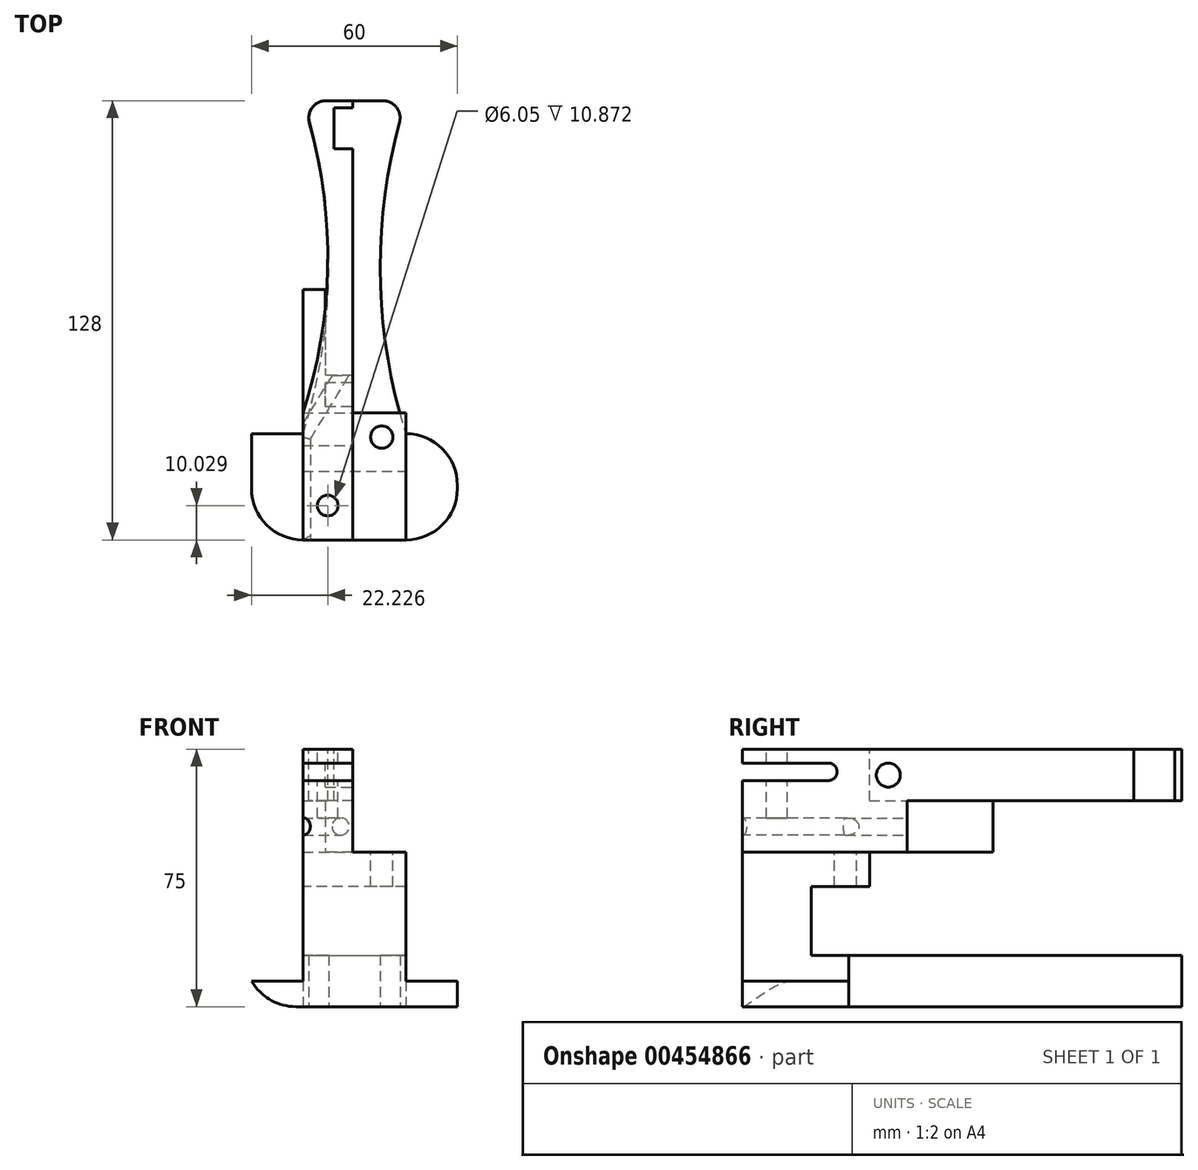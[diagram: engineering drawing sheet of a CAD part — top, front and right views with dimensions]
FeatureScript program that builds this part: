
annotation { "Feature Type Name" : "Feature", "Feature Type Description" : "" }
export const myFeature = defineFeature(function(context is Context, id is Id, definition is map)
    precondition{}
    {
        {
            var Q0;
            Q0=qCreatedBy(makeId("Top.planeOp"),FACE);
            var sketch = newSketch(context, id + "F0", { "sketchPlane" : qUnion([Q0])});
            skLineSegment(sketch, "E0", {"start": v(-15.87, -34.5) * mm, "end": v(-15.87, -0.5) * mm});
            skLineSegment(sketch, "E1", {"start": v(-15.87, -0.5) * mm, "end": v(-15.87, -0.5) * mm});
            skLineSegment(sketch, "E2", {"start": v(14.13, -0.5) * mm, "end": v(14.13, -34.5) * mm});
            skLineSegment(sketch, "E3", {"start": v(14.13, -34.5) * mm, "end": v(-15.87, -34.5) * mm});
            skLineSegment(sketch, "E4", {"start": v(-15.87, -0.5) * mm, "end": v(-15.87, 25.5) * mm});
            skLineSegment(sketch, "E5", {"start": v(-15.87, 25.5) * mm, "end": v(14.13, 25.5) * mm});
            skLineSegment(sketch, "E6", {"start": v(14.13, 25.5) * mm, "end": v(14.13, -0.5) * mm});
            skLineSegment(sketch, "E7.trimOffspring", {"start": v(14.13, -0.5) * mm, "end": v(14.13, -0.5) * mm});
            skLineSegment(sketch, "E8", {"start": v(-0.87, 25.5) * mm, "end": v(-0.87, -34.5) * mm, "construction": true});
            skSolve(sketch);
        }
        {
            var Q0;
            Q0=makeQuery(id+"F0.imprint","IMPRINT",FACE,{"disambiguationData":[TD([[makeQuery(id+"F0.imprint","IMPRINT",EDGE,{"derivedFrom":sQuery(id+"F0.wireOp",EDGE,"E0")}),-1.0]])]});
            extrude(context, id + "F1", {"entities" : qUnion([Q0]), "depth" : 15 * mm});
        }
        {
            var Q0;
            Q0=makeQuery(id+"F1.opExtrude","CAP_FACE",FACE,{"disambiguationData":[OSD([sQuery(id+"F0.wireOp",EDGE,"E0"),sQuery(id+"F0.wireOp",EDGE,"E1"),sQuery(id+"F0.wireOp",EDGE,"E2"),sQuery(id+"F0.wireOp",EDGE,"E3"),sQuery(id+"F0.wireOp",EDGE,"E4"),sQuery(id+"F0.wireOp",EDGE,"E5"),sQuery(id+"F0.wireOp",EDGE,"E6"),sQuery(id+"F0.wireOp",EDGE,"E7.trimOffspring"),sQuery(id+"F0.wireOp",EDGE,"9290abd9-eac5-44e8-944c-73c0075432f2")])],"isStart":false});
            var sketch = newSketch(context, id + "F2", { "sketchPlane" : qUnion([Q0])});
            skLineSegment(sketch, "E9", {"start": v(-15.87, -14.5) * mm, "end": v(14.13, -14.5) * mm});
            skSolve(sketch);
        }
        {
            var Q0;
            Q0 = qSketchRegion(id + "F2", true);
            var Q1;
            {var subQ0=sQuery(id+"F2.wireOp",EDGE,"E9");Q1=makeQuery(id+"F2.imprint","IMPRINT",FACE,{"disambiguationData":[TD([[makeQuery(id+"F2.imprint","IMPRINT",EDGE,{"derivedFrom":subQ0}),-1.0]])]});}
            extrude(context, id + "F3", {"entities" : qUnion([Q0, Q1]), "operationType" : NewBodyOperationType.ADD, "depth" : 30 * mm});
        }
        {
            var Q0;
            Q0=makeQuery(id+"F3.opExtrude","SWEPT_FACE",FACE,{"disambiguationData":[OSD([sQuery(id+"F2.wireOp",EDGE,"E9")])]});
            var sketch = newSketch(context, id + "F4", { "sketchPlane" : qUnion([Q0])});
            skLineSegment(sketch, "E10", {"start": v(-14.13, 35) * mm, "end": v(15.87, 35) * mm});
            skSolve(sketch);
        }
        {
            var Q0;
            {var subQ0=sQuery(id+"F4.wireOp",EDGE,"E10");Q0=makeQuery(id+"F4.imprint","IMPRINT",FACE,{"disambiguationData":[TD([[makeQuery(id+"F4.imprint","IMPRINT",EDGE,{"derivedFrom":subQ0}),1.0]])]});}
            extrude(context, id + "F5", {"entities" : qUnion([Q0]), "operationType" : NewBodyOperationType.ADD, "depth" : 17 * mm});
        }
        {
            var Q0;
            {var subQ0=sQuery(id+"F2.wireOp",EDGE,"E9");Q0=makeQuery(id+"F5.boolean.opBoolean","MERGE",FACE,{"derivedFrom":[makeQuery(id+"F3.opExtrude","CAP_FACE",FACE,{"disambiguationData":[OSD([sQuery(id+"F0.wireOp",EDGE,"E0"),sQuery(id+"F0.wireOp",EDGE,"E2"),sQuery(id+"F0.wireOp",EDGE,"E3"),subQ0])],"isStart":false}),makeQuery(id+"F5.opExtrude","SWEPT_FACE",FACE,{"disambiguationData":[OSD([subQ0])]})]});}
            var sketch = newSketch(context, id + "F6", { "sketchPlane" : qUnion([Q0])});
            skLineSegment(sketch, "E11", {"start": v(-1.37, -34.5) * mm, "end": v(-1.37, -0.5) * mm});
            skLineSegment(sketch, "E12", {"start": v(-1.37, -0.5) * mm, "end": v(-15.87, -0.5) * mm});
            skSolve(sketch);
        }
        {
            var Q0;
            {var subQ0=sQuery(id+"F6.wireOp",EDGE,"E11");Q0=makeQuery(id+"F6.imprint","IMPRINT",FACE,{"disambiguationData":[TD([[makeQuery(id+"F6.imprint","IMPRINT",EDGE,{"derivedFrom":subQ0}),1.0]])]});}
            extrude(context, id + "F7", {"entities" : qUnion([Q0]), "operationType" : NewBodyOperationType.ADD, "depth" : 30 * mm});
        }
        {
            var Q0;
            Q0=makeQuery(id+"F7.opExtrude","SWEPT_FACE",FACE,{"disambiguationData":[OSD([sQuery(id+"F6.wireOp",EDGE,"E11")])]});
            var sketch = newSketch(context, id + "F8", { "sketchPlane" : qUnion([Q0])});
            skLineSegment(sketch, "E13", {"start": v(-34.5, 71) * mm, "end": v(-9.5, 71) * mm});
            skLineSegment(sketch, "E14", {"start": v(-34.5, 65.87) * mm, "end": v(-9.5, 65.87) * mm});
            skArc(sketch, "E15", {"start": v(-9.5, 65.87) * mm, "mid": v(-6.94, 68.44) * mm, "end": v(-9.5, 71) * mm});
            skSolve(sketch);
        }
        {
            var Q0;
            Q0 = qSketchRegion(id + "F8", true);
            var Q1;
            {var subQ0=sQuery(id+"F8.wireOp",EDGE,"E13");Q1=makeQuery(id+"F8.imprint","IMPRINT",FACE,{"disambiguationData":[TD([[makeQuery(id+"F8.imprint","IMPRINT",EDGE,{"derivedFrom":subQ0}),-1.0]])]});}
            extrude(context, id + "F9", {"entities" : qUnion([Q0, Q1]), "operationType" : NewBodyOperationType.REMOVE, "oppositeDirection" : true, "depth" : 15 * mm});
        }
        {
            var Q0;
            Q0=makeQuery(id+"F7.opExtrude","SWEPT_FACE",FACE,{"disambiguationData":[OSD([sQuery(id+"F6.wireOp",EDGE,"E12")])]});
            var sketch = newSketch(context, id + "F10", { "sketchPlane" : qUnion([Q0])});
            skLineSegment(sketch, "E16", {"start": v(6.37, 45) * mm, "end": v(6.37, 60) * mm});
            skLineSegment(sketch, "E17", {"start": v(6.37, 60) * mm, "end": v(15.87, 60) * mm});
            skLineSegment(sketch, "E18", {"start": v(6.37, 60) * mm, "end": v(6.37, 75) * mm});
            skLineSegment(sketch, "E19", {"start": v(15.87, 75) * mm, "end": v(15.87, 60) * mm});
            skSolve(sketch);
        }
        {
            var Q0;
            {var subQ4=sQuery(id+"F10.wireOp",EDGE,"E16");Q0=makeQuery(id+"F10.imprint","IMPRINT",FACE,{"disambiguationData":[TD([[makeQuery(id+"F10.imprint","IMPRINT",EDGE,{"derivedFrom":subQ4}),1.0]])]});}
            extrude(context, id + "F11", {"entities" : qUnion([Q0]), "operationType" : NewBodyOperationType.ADD, "depth" : 14 * mm});
        }
        {
            var Q0;
            {var subQ7=sQuery(id+"F10.wireOp",EDGE,"E16");Q0=makeQuery(id+"F10.imprint","IMPRINT",FACE,{"disambiguationData":[TD([[makeQuery(id+"F10.imprint","IMPRINT",EDGE,{"derivedFrom":subQ7}),-1.0]])]});}
            extrude(context, id + "F12", {"entities" : qUnion([Q0]), "operationType" : NewBodyOperationType.ADD, "depth" : 14 * mm});
        }
        {
            var Q0;
            {var subQ0=sQuery(id+"F10.wireOp",EDGE,"E18");Q0=makeQuery(id+"F10.imprint","IMPRINT",FACE,{"disambiguationData":[TD([[makeQuery(id+"F10.imprint","IMPRINT",EDGE,{"derivedFrom":subQ0}),-1.0]])]});}
            extrude(context, id + "F13", {"entities" : qUnion([Q0]), "operationType" : NewBodyOperationType.ADD, "depth" : 14 * mm});
        }
        {
            var Q0;
            {var subQ0=sQuery(id+"F6.wireOp",EDGE,"E11");Q0=makeQuery(id+"F11.boolean.opBoolean","MERGE",FACE,{"derivedFrom":[makeQuery(id+"F7.opExtrude","SWEPT_FACE",FACE,{"disambiguationData":[OSD([subQ0])]}),makeQuery(id+"F11.opExtrude","SWEPT_FACE",FACE,{"disambiguationData":[OSD([subQ0,sQuery(id+"F6.wireOp",EDGE,"E12")])]})]});}
            var sketch = newSketch(context, id + "F14", { "sketchPlane" : qUnion([Q0])});
            skCircle(sketch, "E20", {"center": v(8, 67.5) * mm, "radius": 3.5 * mm});
            skSolve(sketch);
        }
        {
            var Q0;
            Q0=makeQuery(id+"F14.imprint","IMPRINT",FACE,{"disambiguationData":[TD([[makeQuery(id+"F14.imprint","IMPRINT",EDGE,{"derivedFrom":sQuery(id+"F14.wireOp",EDGE,"E20")}),1.0]])]});
            extrude(context, id + "F15", {"entities" : qUnion([Q0]), "operationType" : NewBodyOperationType.REMOVE, "oppositeDirection" : true, "depth" : 8 * mm});
        }
        {
            var Q0;
            {var subQ0=sQuery(id+"F0.wireOp",EDGE,"E3");var subQ4=sQuery(id+"F0.wireOp",EDGE,"E2");var subQ5=sQuery(id+"F2.wireOp",EDGE,"E9");var subQ6=sQuery(id+"F0.wireOp",EDGE,"E0");Q0=makeQuery(id+"F11.boolean.opBoolean","SPLIT",FACE,{"disambiguationData":[TD([makeQuery(id+"F1.opExtrude","SWEPT_FACE",FACE,{"disambiguationData":[OSD([subQ4])]})])],"derivedFrom":makeQuery(id+"F5.boolean.opBoolean","MERGE",FACE,{"derivedFrom":[makeQuery(id+"F3.opExtrude","CAP_FACE",FACE,{"disambiguationData":[OSD([subQ6,subQ4,subQ0,subQ5])],"isStart":false}),makeQuery(id+"F5.opExtrude","SWEPT_FACE",FACE,{"disambiguationData":[OSD([subQ5])]})]})});}
            var sketch = newSketch(context, id + "F16", { "sketchPlane" : qUnion([Q0])});
            skCircle(sketch, "E21", {"center": v(7.1, -4.53) * mm, "radius": 3.25 * mm});
            skSolve(sketch);
        }
        {
            var Q0;
            Q0=makeQuery(id+"F16.imprint","IMPRINT",FACE,{"disambiguationData":[TD([[makeQuery(id+"F16.imprint","IMPRINT",EDGE,{"derivedFrom":sQuery(id+"F16.wireOp",EDGE,"E21")}),1.0]])]});
            extrude(context, id + "F17", {"entities" : qUnion([Q0]), "operationType" : NewBodyOperationType.REMOVE, "oppositeDirection" : true, "depth" : 25 * mm});
        }
        {
            var Q0;
            {var subQ0=sQuery(id+"F6.wireOp",EDGE,"E12");var subQ1=makeQuery(id+"F7.opExtrude","CAP_EDGE",EDGE,{"disambiguationData":[OSD([subQ0])],"isStart":false});var subQ2=sQuery(id+"F6.wireOp",EDGE,"E11");Q0=makeQuery(id+"F13.boolean.opBoolean","MERGE",FACE,{"derivedFrom":[makeQuery(id+"F11.boolean.opBoolean","MERGE",FACE,{"derivedFrom":[makeQuery(id+"F7.opExtrude","CAP_FACE",FACE,{"disambiguationData":[OSD([sQuery(id+"F0.wireOp",EDGE,"E0"),sQuery(id+"F0.wireOp",EDGE,"E3"),sQuery(id+"F2.wireOp",EDGE,"E9"),subQ2,subQ0])],"isStart":false}),makeQuery(id+"F11.opExtrude","SWEPT_FACE",FACE,{"disambiguationData":[OSD([subQ0]),TDD([makeQuery(id+"F10.imprint","IMPRINT",EDGE,{"disambiguationData":[TD([[makeQuery(id+"F10.imprint","INTERSECT",VERTEX,{"derivedFrom":[subQ1,sQuery(id+"F10.wireOp",EDGE,"E18")]}),1.0]])],"derivedFrom":subQ1})])]})]}),makeQuery(id+"F13.opExtrude","SWEPT_FACE",FACE,{"disambiguationData":[OSD([subQ0])]})]});}
            var sketch = newSketch(context, id + "F18", { "sketchPlane" : qUnion([Q0])});
            skCircle(sketch, "E22", {"center": v(-8.64, -24.48) * mm, "radius": 3.02 * mm});
            skSolve(sketch);
        }
        {
            var Q0;
            {var subQ0=sQuery(id+"F10.wireOp",EDGE,"E18");var subQ1=sQuery(id+"F10.wireOp",EDGE,"E17");var subQ2=sQuery(id+"F6.wireOp",EDGE,"E12");var subQ3=sQuery(id+"F10.wireOp",EDGE,"E16");Q0=makeQuery(id+"F13.boolean.opBoolean","MERGE",FACE,{"derivedFrom":[makeQuery(id+"F12.boolean.opBoolean","MERGE",FACE,{"derivedFrom":[makeQuery(id+"F11.opExtrude","CAP_FACE",FACE,{"disambiguationData":[OSD([sQuery(id+"F6.wireOp",EDGE,"E11"),subQ2,subQ3,subQ0])],"isStart":false}),makeQuery(id+"F12.opExtrude","CAP_FACE",FACE,{"disambiguationData":[OSD([sQuery(id+"F0.wireOp",EDGE,"E0"),sQuery(id+"F2.wireOp",EDGE,"E9"),subQ2,subQ3,subQ1])],"isStart":false})]}),makeQuery(id+"F13.opExtrude","CAP_FACE",FACE,{"disambiguationData":[OSD([subQ2,subQ1,subQ0,sQuery(id+"F10.wireOp",EDGE,"E19")])],"isStart":false})]});}
            var sketch = newSketch(context, id + "F19", { "sketchPlane" : qUnion([Q0])});
            skLineSegment(sketch, "E23", {"start": v(1.37, 60) * mm, "end": v(15.87, 60) * mm});
            skSolve(sketch);
        }
        {
            var Q0;
            {var subQ0=sQuery(id+"F19.wireOp",EDGE,"E23");Q0=makeQuery(id+"F19.imprint","IMPRINT",FACE,{"disambiguationData":[TD([[makeQuery(id+"F19.imprint","IMPRINT",EDGE,{"derivedFrom":subQ0}),1.0]])]});}
            extrude(context, id + "F20", {"entities" : qUnion([Q0]), "operationType" : NewBodyOperationType.ADD, "depth" : 80 * mm});
        }
        {
            var Q0;
            {var subQ0=sQuery(id+"F6.wireOp",EDGE,"E12");var subQ1=makeQuery(id+"F7.opExtrude","CAP_EDGE",EDGE,{"disambiguationData":[OSD([subQ0])],"isStart":false});var subQ2=sQuery(id+"F6.wireOp",EDGE,"E11");Q0=makeQuery(id+"F20.boolean.opBoolean","MERGE",FACE,{"derivedFrom":[makeQuery(id+"F13.boolean.opBoolean","MERGE",FACE,{"derivedFrom":[makeQuery(id+"F11.boolean.opBoolean","MERGE",FACE,{"derivedFrom":[makeQuery(id+"F7.opExtrude","CAP_FACE",FACE,{"disambiguationData":[OSD([sQuery(id+"F0.wireOp",EDGE,"E0"),sQuery(id+"F0.wireOp",EDGE,"E3"),sQuery(id+"F2.wireOp",EDGE,"E9"),subQ2,subQ0])],"isStart":false}),makeQuery(id+"F11.opExtrude","SWEPT_FACE",FACE,{"disambiguationData":[OSD([subQ0]),TDD([makeQuery(id+"F10.imprint","IMPRINT",EDGE,{"disambiguationData":[TD([[makeQuery(id+"F10.imprint","INTERSECT",VERTEX,{"derivedFrom":[subQ1,sQuery(id+"F10.wireOp",EDGE,"E18")]}),1.0]])],"derivedFrom":subQ1})])]})]}),makeQuery(id+"F13.opExtrude","SWEPT_FACE",FACE,{"disambiguationData":[OSD([subQ0])]})]}),makeQuery(id+"F20.opExtrude","SWEPT_FACE",FACE,{"disambiguationData":[OSD([subQ0])]})]});}
            var sketch = newSketch(context, id + "F21", { "sketchPlane" : qUnion([Q0])});
            skLineSegment(sketch, "E24", {"start": v(-1.37, 2.5) * mm, "end": v(-15.87, 2.5) * mm});
            skArc(sketch, "E25", {"start": v(-15.87, 2.5) * mm, "mid": v(-8.62, 48) * mm, "end": v(-15.87, 93.5) * mm});
            skSolve(sketch);
        }
        {
            var Q0;
            {var subQ0=sQuery(id+"F21.wireOp",EDGE,"E25");Q0=makeQuery(id+"F21.imprint","IMPRINT",FACE,{"disambiguationData":[TD([[makeQuery(id+"F21.imprint","IMPRINT",EDGE,{"derivedFrom":subQ0}),1.0]])]});}
            extrude(context, id + "F22", {"entities" : qUnion([Q0]), "operationType" : NewBodyOperationType.REMOVE, "oppositeDirection" : true, "depth" : 15 * mm});
        }
        {
            var Q0;
            {var subQ0=sQuery(id+"F6.wireOp",EDGE,"E12");var subQ1=makeQuery(id+"F7.opExtrude","CAP_EDGE",EDGE,{"disambiguationData":[OSD([subQ0])],"isStart":false});var subQ2=sQuery(id+"F6.wireOp",EDGE,"E11");Q0=makeQuery(id+"F20.boolean.opBoolean","MERGE",FACE,{"derivedFrom":[makeQuery(id+"F13.boolean.opBoolean","MERGE",FACE,{"derivedFrom":[makeQuery(id+"F11.boolean.opBoolean","MERGE",FACE,{"derivedFrom":[makeQuery(id+"F7.opExtrude","CAP_FACE",FACE,{"disambiguationData":[OSD([sQuery(id+"F0.wireOp",EDGE,"E0"),sQuery(id+"F0.wireOp",EDGE,"E3"),sQuery(id+"F2.wireOp",EDGE,"E9"),subQ2,subQ0])],"isStart":false}),makeQuery(id+"F11.opExtrude","SWEPT_FACE",FACE,{"disambiguationData":[OSD([subQ0]),TDD([makeQuery(id+"F10.imprint","IMPRINT",EDGE,{"disambiguationData":[TD([[makeQuery(id+"F10.imprint","INTERSECT",VERTEX,{"derivedFrom":[subQ1,sQuery(id+"F10.wireOp",EDGE,"E18")]}),1.0]])],"derivedFrom":subQ1})])]})]}),makeQuery(id+"F13.opExtrude","SWEPT_FACE",FACE,{"disambiguationData":[OSD([subQ0])]})]}),makeQuery(id+"F20.opExtrude","SWEPT_FACE",FACE,{"disambiguationData":[OSD([subQ0])]})]});}
            var sketch = newSketch(context, id + "F23", { "sketchPlane" : qUnion([Q0])});
            skLineSegment(sketch, "E26.bottom", {"start": v(-1.37, 91.5) * mm, "end": v(-6.87, 91.5) * mm});
            skLineSegment(sketch, "E26.top", {"start": v(-1.37, 79.5) * mm, "end": v(-6.87, 79.5) * mm});
            skLineSegment(sketch, "E26.left", {"start": v(-1.37, 91.5) * mm, "end": v(-1.37, 79.5) * mm});
            skLineSegment(sketch, "E26.right", {"start": v(-6.87, 91.5) * mm, "end": v(-6.87, 79.5) * mm});
            skSolve(sketch);
        }
        {
            var Q0;
            Q0=makeQuery(id+"F23.imprint","IMPRINT",FACE,{"disambiguationData":[TD([[makeQuery(id+"F23.imprint","IMPRINT",EDGE,{"derivedFrom":sQuery(id+"F23.wireOp",EDGE,"E26.bottom")}),1.0]])]});
            extrude(context, id + "F24", {"entities" : qUnion([Q0]), "operationType" : NewBodyOperationType.REMOVE, "oppositeDirection" : true, "depth" : 15 * mm});
        }
        {
            var Q0;
            Q0=makeQuery(id+"F1.opExtrude","SWEPT_FACE",FACE,{"disambiguationData":[OSD([sQuery(id+"F0.wireOp",EDGE,"E5")])]});
            extrude(context, id + "F25", {"entities" : qUnion([Q0]), "operationType" : NewBodyOperationType.ADD, "depth" : 68 * mm});
        }
        {
            var Q0;
            {var subQ0=sQuery(id+"F0.wireOp",EDGE,"E5");Q0=makeQuery(id+"F25.boolean.opBoolean","MERGE",FACE,{"derivedFrom":[makeQuery(id+"F1.opExtrude","CAP_FACE",FACE,{"disambiguationData":[OSD([sQuery(id+"F0.wireOp",EDGE,"E0"),sQuery(id+"F0.wireOp",EDGE,"E2"),sQuery(id+"F0.wireOp",EDGE,"E3"),sQuery(id+"F0.wireOp",EDGE,"E4"),subQ0,sQuery(id+"F0.wireOp",EDGE,"E6")])],"isStart":true}),makeQuery(id+"F25.opExtrude","SWEPT_FACE",FACE,{"disambiguationData":[OSD([subQ0]),TDD([makeQuery(id+"F1.opExtrude","CAP_EDGE",EDGE,{"disambiguationData":[OSD([subQ0])],"isStart":true})])]})]});}
            var sketch = newSketch(context, id + "F26", { "sketchPlane" : qUnion([Q0])});
            skArc(sketch, "E27", {"start": v(-15.87, -93.5) * mm, "mid": v(-8.37, -45) * mm, "end": v(-15.87, 3.5) * mm});
            skArc(sketch, "E28", {"start": v(14.13, 3.5) * mm, "mid": v(6.63, -45) * mm, "end": v(14.13, -93.5) * mm});
            skSolve(sketch);
        }
        {
            var Q0;
            {var subQ0=sQuery(id+"F26.wireOp",EDGE,"E27");Q0=makeQuery(id+"F26.imprint","IMPRINT",FACE,{"disambiguationData":[TD([[makeQuery(id+"F26.imprint","IMPRINT",EDGE,{"derivedFrom":subQ0}),1.0]])]});}
            var Q1;
            {var subQ0=sQuery(id+"F26.wireOp",EDGE,"E28");Q1=makeQuery(id+"F26.imprint","IMPRINT",FACE,{"disambiguationData":[TD([[makeQuery(id+"F26.imprint","IMPRINT",EDGE,{"derivedFrom":subQ0}),1.0]])]});}
            extrude(context, id + "F27", {"entities" : qUnion([Q0, Q1]), "operationType" : NewBodyOperationType.REMOVE, "oppositeDirection" : true, "depth" : 15 * mm});
        }
        {
            var Q0;
            {var subQ0=sQuery(id+"F26.wireOp",EDGE,"E27");var subQ1=sQuery(id+"F0.wireOp",EDGE,"E5");var subQ2=sQuery(id+"F0.wireOp",EDGE,"E4");var subQ3=sQuery(id+"F0.wireOp",EDGE,"E0");Q0=makeQuery(id+"F27.boolean.opBoolean","MERGE",EDGE,{"derivedFrom":[makeQuery(id+"F25.opExtrude","CAP_EDGE",EDGE,{"disambiguationData":[OSD([subQ2,subQ1])],"isStart":false}),makeQuery(id+"F27.opExtrude","SWEPT_EDGE",EDGE,{"disambiguationData":[OSD([subQ3,subQ2,subQ1,subQ0]),TDD([makeQuery(id+"F26.imprint","INTERSECT",VERTEX,{"derivedFrom":[makeQuery(id+"F25.opExtrude","CAP_EDGE",EDGE,{"disambiguationData":[OSD([subQ1]),TDD([makeQuery(id+"F1.opExtrude","CAP_EDGE",EDGE,{"disambiguationData":[OSD([subQ1])],"isStart":true})])],"isStart":false}),makeQuery(id+"F25.boolean.opBoolean","MERGE",EDGE,{"derivedFrom":[makeQuery(id+"F1.opExtrude","CAP_EDGE",EDGE,{"disambiguationData":[OSD([subQ3,subQ2])],"isStart":true}),makeQuery(id+"F25.opExtrude","SWEPT_EDGE",EDGE,{"disambiguationData":[OSD([subQ2,subQ1]),TDD([makeQuery(id+"F1.opExtrude","CAP_VERTEX",VERTEX,{"disambiguationData":[OSD([subQ2,subQ1])],"isStart":true})])]})]}),subQ0]})])]})]});}
            var Q1;
            {var subQ0=sQuery(id+"F10.wireOp",EDGE,"E19");var subQ1=sQuery(id+"F6.wireOp",EDGE,"E12");var subQ2=sQuery(id+"F2.wireOp",EDGE,"E9");var subQ3=sQuery(id+"F0.wireOp",EDGE,"E4");var subQ4=sQuery(id+"F0.wireOp",EDGE,"E0");Q1=makeQuery(id+"F22.boolean.opBoolean","MERGE",EDGE,{"derivedFrom":[makeQuery(id+"F20.opExtrude","CAP_EDGE",EDGE,{"disambiguationData":[OSD([subQ4,subQ3,subQ2,subQ1,subQ0])],"isStart":false}),makeQuery(id+"F22.opExtrude","SWEPT_EDGE",EDGE,{"disambiguationData":[OSD([subQ4,subQ3,subQ2,subQ1,subQ0,sQuery(id+"F21.wireOp",EDGE,"E25")])]})]});}
            var Q2;
            {var subQ0=sQuery(id+"F26.wireOp",EDGE,"E28");var subQ1=sQuery(id+"F0.wireOp",EDGE,"E6");var subQ2=sQuery(id+"F0.wireOp",EDGE,"E5");var subQ3=sQuery(id+"F0.wireOp",EDGE,"E2");Q2=makeQuery(id+"F27.boolean.opBoolean","MERGE",EDGE,{"derivedFrom":[makeQuery(id+"F25.opExtrude","CAP_EDGE",EDGE,{"disambiguationData":[OSD([subQ2,subQ1])],"isStart":false}),makeQuery(id+"F27.opExtrude","SWEPT_EDGE",EDGE,{"disambiguationData":[OSD([subQ3,subQ2,subQ1,subQ0]),TDD([makeQuery(id+"F26.imprint","INTERSECT",VERTEX,{"derivedFrom":[makeQuery(id+"F25.opExtrude","CAP_EDGE",EDGE,{"disambiguationData":[OSD([subQ2]),TDD([makeQuery(id+"F1.opExtrude","CAP_EDGE",EDGE,{"disambiguationData":[OSD([subQ2])],"isStart":true})])],"isStart":false}),makeQuery(id+"F25.boolean.opBoolean","MERGE",EDGE,{"derivedFrom":[makeQuery(id+"F1.opExtrude","CAP_EDGE",EDGE,{"disambiguationData":[OSD([subQ3,subQ1])],"isStart":true}),makeQuery(id+"F25.opExtrude","SWEPT_EDGE",EDGE,{"disambiguationData":[OSD([subQ2,subQ1]),TDD([makeQuery(id+"F1.opExtrude","CAP_VERTEX",VERTEX,{"disambiguationData":[OSD([subQ2,subQ1])],"isStart":true})])]})]}),subQ0]})])]})]});}
            fillet(context, id + "F28", {"entities" : qUnion([Q0, Q1, Q2]), "radius" : 5 * mm, "tangentPropagation" : true, "allowEdgeOverflow" : false});
        }
        {
            var Q0;
            {var subQ0=sQuery(id+"F10.wireOp",EDGE,"E18");var subQ1=sQuery(id+"F10.wireOp",EDGE,"E17");var subQ2=sQuery(id+"F6.wireOp",EDGE,"E12");var subQ3=sQuery(id+"F10.wireOp",EDGE,"E16");Q0=makeQuery(id+"F13.boolean.opBoolean","MERGE",FACE,{"derivedFrom":[makeQuery(id+"F12.boolean.opBoolean","MERGE",FACE,{"derivedFrom":[makeQuery(id+"F11.opExtrude","CAP_FACE",FACE,{"disambiguationData":[OSD([sQuery(id+"F6.wireOp",EDGE,"E11"),subQ2,subQ3,subQ0])],"isStart":false}),makeQuery(id+"F12.opExtrude","CAP_FACE",FACE,{"disambiguationData":[OSD([sQuery(id+"F0.wireOp",EDGE,"E0"),sQuery(id+"F0.wireOp",EDGE,"E4"),sQuery(id+"F2.wireOp",EDGE,"E9"),subQ2,subQ3,subQ1])],"isStart":false})]}),makeQuery(id+"F13.opExtrude","CAP_FACE",FACE,{"disambiguationData":[OSD([subQ2,subQ1,subQ0,sQuery(id+"F10.wireOp",EDGE,"E19")])],"isStart":false})]});}
            var sketch = newSketch(context, id + "F29", { "sketchPlane" : qUnion([Q0])});
            skLineSegment(sketch, "E29", {"start": v(9.37, 60) * mm, "end": v(9.37, 45) * mm});
            skSolve(sketch);
        }
        {
            var Q0;
            {var subQ18=sQuery(id+"F29.wireOp",EDGE,"E29");Q0=makeQuery(id+"F29.imprint","IMPRINT",FACE,{"disambiguationData":[TD([[makeQuery(id+"F29.imprint","IMPRINT",EDGE,{"derivedFrom":subQ18}),1.0]])]});}
            extrude(context, id + "F30", {"entities" : qUnion([Q0]), "operationType" : NewBodyOperationType.ADD, "depth" : 45 * mm});
        }
        {
            var Q0;
            Q0=makeQuery(id+"F18.imprint","IMPRINT",FACE,{"disambiguationData":[TD([[makeQuery(id+"F18.imprint","IMPRINT",EDGE,{"derivedFrom":sQuery(id+"F18.wireOp",EDGE,"E22")}),1.0]])]});
            extrude(context, id + "F31", {"entities" : qUnion([Q0]), "operationType" : NewBodyOperationType.REMOVE, "oppositeDirection" : true, "depth" : 20 * mm});
        }
        {
            var Q0;
            Q0=qCreatedBy(makeId("Top.planeOp"),FACE);
            cPlane(context, id + "F32", {"entities" : qUnion([Q0]), "cplaneType" : CPlaneType.OFFSET, "offset" : 52.5 * mm, "width" : 150 * mm, "height" : 150 * mm});
        }
        {
            var Q0;
            Q0=qCreatedBy(id+"F32.planeOp",FACE);
            var sketch = newSketch(context, id + "F33", { "sketchPlane" : qUnion([Q0])});
            skLineSegment(sketch, "E30", {"start": v(0, -34.5) * mm, "end": v(-15.87, -34.5) * mm});
            skLineSegment(sketch, "E31", {"start": v(-15.87, -34.5) * mm, "end": v(-15.87, -4.5) * mm});
            skLineSegment(sketch, "E32", {"start": v(-15.89, 13.5) * mm, "end": v(-4.89, 13.5) * mm});
            skLineSegment(sketch, "E33", {"start": v(-15.87, -4.5) * mm, "end": v(-4.89, 13.5) * mm});
            skLineSegment(sketch, "E34", {"start": v(-15.87, -34.5) * mm, "end": v(-15.87, -35.92) * mm});
            skSolve(sketch);
        }
        {
            var Q0;
            {var subQ0=sQuery(id+"F10.wireOp",EDGE,"E18");var subQ1=sQuery(id+"F10.wireOp",EDGE,"E17");var subQ2=sQuery(id+"F6.wireOp",EDGE,"E12");var subQ3=sQuery(id+"F10.wireOp",EDGE,"E16");Q0=makeQuery(id+"F13.boolean.opBoolean","MERGE",FACE,{"derivedFrom":[makeQuery(id+"F12.boolean.opBoolean","MERGE",FACE,{"derivedFrom":[makeQuery(id+"F11.opExtrude","CAP_FACE",FACE,{"disambiguationData":[OSD([sQuery(id+"F6.wireOp",EDGE,"E11"),subQ2,subQ3,subQ0])],"isStart":false}),makeQuery(id+"F12.opExtrude","CAP_FACE",FACE,{"disambiguationData":[OSD([sQuery(id+"F0.wireOp",EDGE,"E0"),sQuery(id+"F0.wireOp",EDGE,"E4"),sQuery(id+"F2.wireOp",EDGE,"E9"),subQ2,subQ3,subQ1])],"isStart":false})]}),makeQuery(id+"F13.opExtrude","CAP_FACE",FACE,{"disambiguationData":[OSD([subQ2,subQ1,subQ0,sQuery(id+"F10.wireOp",EDGE,"E19")])],"isStart":false})]});}
            var sketch = newSketch(context, id + "F34", { "sketchPlane" : qUnion([Q0])});
            skCircle(sketch, "E35", {"center": v(4.87, 52.5) * mm, "radius": 2.5 * mm});
            skSolve(sketch);
        }
        {
            var Q0;
            Q0=makeQuery(id+"F34.imprint","IMPRINT",FACE,{"disambiguationData":[TD([[makeQuery(id+"F34.imprint","IMPRINT",EDGE,{"derivedFrom":sQuery(id+"F34.wireOp",EDGE,"E35")}),1.0]])]});
            var Q1;
            Q1=sQuery(id+"F33.wireOp",EDGE,"E33");
            var Q2;
            Q2=sQuery(id+"F33.wireOp",EDGE,"E31");
            var Q3;
            Q3=sQuery(id+"F33.wireOp",EDGE,"E34");
            sweep(context, id + "F35", {"operationType" : NewBodyOperationType.REMOVE, "profiles" : qUnion([Q0]), "path" : qUnion([Q1, Q2, Q3])});
        }
        {
            var Q0;
            {var subQ0=sQuery(id+"F10.wireOp",EDGE,"E19");var subQ1=sQuery(id+"F6.wireOp",EDGE,"E12");var subQ2=sQuery(id+"F2.wireOp",EDGE,"E9");var subQ3=sQuery(id+"F0.wireOp",EDGE,"E4");var subQ4=sQuery(id+"F0.wireOp",EDGE,"E0");Q0=makeQuery(id+"F30.boolean.opBoolean","MERGE",FACE,{"derivedFrom":[makeQuery(id+"F25.boolean.opBoolean","MERGE",FACE,{"derivedFrom":[makeQuery(id+"F20.boolean.opBoolean","MERGE",FACE,{"derivedFrom":[makeQuery(id+"F13.boolean.opBoolean","MERGE",FACE,{"derivedFrom":[makeQuery(id+"F12.boolean.opBoolean","MERGE",FACE,{"derivedFrom":[makeQuery(id+"F7.boolean.opBoolean","MERGE",FACE,{"derivedFrom":[makeQuery(id+"F5.boolean.opBoolean","MERGE",FACE,{"derivedFrom":[makeQuery(id+"F3.boolean.opBoolean","MERGE",FACE,{"derivedFrom":[makeQuery(id+"F1.opExtrude","SWEPT_FACE",FACE,{"disambiguationData":[OSD([subQ4,subQ3])]}),makeQuery(id+"F3.opExtrude","SWEPT_FACE",FACE,{"disambiguationData":[OSD([subQ4,subQ3])]})]}),makeQuery(id+"F5.opExtrude","SWEPT_FACE",FACE,{"disambiguationData":[OSD([subQ4,subQ3,subQ2])]})]}),makeQuery(id+"F7.opExtrude","SWEPT_FACE",FACE,{"disambiguationData":[OSD([subQ4,subQ3,subQ2])]})]}),makeQuery(id+"F12.opExtrude","SWEPT_FACE",FACE,{"disambiguationData":[OSD([subQ4,subQ3,subQ2,subQ1])]})]}),makeQuery(id+"F13.opExtrude","SWEPT_FACE",FACE,{"disambiguationData":[OSD([subQ0])]})]}),makeQuery(id+"F20.opExtrude","SWEPT_FACE",FACE,{"disambiguationData":[OSD([subQ4,subQ3,subQ2,subQ1,subQ0])]})]}),makeQuery(id+"F25.opExtrude","SWEPT_FACE",FACE,{"disambiguationData":[OSD([subQ3,sQuery(id+"F0.wireOp",EDGE,"E5")])]})]}),makeQuery(id+"F30.opExtrude","SWEPT_FACE",FACE,{"disambiguationData":[OSD([subQ4,subQ3,subQ2,subQ1,subQ0])]})]});}
            var sketch = newSketch(context, id + "F36", { "sketchPlane" : qUnion([Q0])});
            skLineSegment(sketch, "E36", {"start": v(3.5, 7.5) * mm, "end": v(34.5, 7.5) * mm});
            skSolve(sketch);
        }
        {
            var Q0;
            {var subQ0=sQuery(id+"F36.wireOp",EDGE,"E36");Q0=makeQuery(id+"F36.imprint","IMPRINT",FACE,{"disambiguationData":[TD([[makeQuery(id+"F36.imprint","IMPRINT",EDGE,{"derivedFrom":subQ0}),-1.0]])]});}
            extrude(context, id + "F37", {"entities" : qUnion([Q0]), "operationType" : NewBodyOperationType.ADD, "depth" : 15 * mm});
        }
        {
            var Q0;
            {var subQ0=sQuery(id+"F0.wireOp",EDGE,"E6");var subQ1=sQuery(id+"F0.wireOp",EDGE,"E2");Q0=makeQuery(id+"F25.boolean.opBoolean","MERGE",FACE,{"derivedFrom":[makeQuery(id+"F5.boolean.opBoolean","MERGE",FACE,{"derivedFrom":[makeQuery(id+"F3.boolean.opBoolean","MERGE",FACE,{"derivedFrom":[makeQuery(id+"F1.opExtrude","SWEPT_FACE",FACE,{"disambiguationData":[OSD([subQ1,subQ0])]}),makeQuery(id+"F3.opExtrude","SWEPT_FACE",FACE,{"disambiguationData":[OSD([subQ1,subQ0])]})]}),makeQuery(id+"F5.opExtrude","SWEPT_FACE",FACE,{"disambiguationData":[OSD([subQ1,subQ0,sQuery(id+"F2.wireOp",EDGE,"E9")])]})]}),makeQuery(id+"F25.opExtrude","SWEPT_FACE",FACE,{"disambiguationData":[OSD([sQuery(id+"F0.wireOp",EDGE,"E5"),subQ0])]})]});}
            var sketch = newSketch(context, id + "F38", { "sketchPlane" : qUnion([Q0])});
            skLineSegment(sketch, "E37", {"start": v(-3.5, 7.5) * mm, "end": v(-34.5, 7.5) * mm});
            skSolve(sketch);
        }
        {
            var Q0;
            {var subQ0=sQuery(id+"F38.wireOp",EDGE,"E37");Q0=makeQuery(id+"F38.imprint","IMPRINT",FACE,{"disambiguationData":[TD([[makeQuery(id+"F38.imprint","IMPRINT",EDGE,{"derivedFrom":subQ0}),1.0]])]});}
            extrude(context, id + "F39", {"entities" : qUnion([Q0]), "operationType" : NewBodyOperationType.ADD, "depth" : 15 * mm});
        }
        {
            var Q0;
            Q0=makeQuery(id+"F39.opExtrude","CAP_EDGE",EDGE,{"disambiguationData":[OSD([sQuery(id+"F0.wireOp",EDGE,"E2"),sQuery(id+"F0.wireOp",EDGE,"E3"),sQuery(id+"F0.wireOp",EDGE,"E6")])],"isStart":false});
            var Q1;
            Q1=makeQuery(id+"F39.opExtrude","CAP_EDGE",EDGE,{"disambiguationData":[OSD([sQuery(id+"F0.wireOp",EDGE,"E2"),sQuery(id+"F0.wireOp",EDGE,"E5"),sQuery(id+"F0.wireOp",EDGE,"E6"),sQuery(id+"F26.wireOp",EDGE,"E28")])],"isStart":false});
            var Q2;
            Q2=makeQuery(id+"F37.opExtrude","CAP_EDGE",EDGE,{"disambiguationData":[OSD([sQuery(id+"F0.wireOp",EDGE,"E0"),sQuery(id+"F0.wireOp",EDGE,"E4"),sQuery(id+"F0.wireOp",EDGE,"E5"),sQuery(id+"F26.wireOp",EDGE,"E27")])],"isStart":false});
            var Q3;
            Q3=makeQuery(id+"F37.opExtrude","CAP_EDGE",EDGE,{"disambiguationData":[OSD([sQuery(id+"F0.wireOp",EDGE,"E0"),sQuery(id+"F0.wireOp",EDGE,"E3"),sQuery(id+"F0.wireOp",EDGE,"E4"),sQuery(id+"F2.wireOp",EDGE,"E9")])],"isStart":false});
            fillet(context, id + "F40", {"entities" : qUnion([Q0, Q1, Q2, Q3]), "radius" : 15 * mm, "tangentPropagation" : true, "allowEdgeOverflow" : false});
        }
        {
            var Q0;
            Q0=makeQuery(id+"F30.opExtrude","SWEPT_FACE",FACE,{"disambiguationData":[OSD([sQuery(id+"F29.wireOp",EDGE,"E29")])]});
            var sketch = newSketch(context, id + "F41", { "sketchPlane" : qUnion([Q0])});
            skLineSegment(sketch, "E38", {"start": v(13.5, 52.5) * mm, "end": v(38.5, 52.5) * mm});
            skPoint(sketch, "E38.endSnap0", {"position": v(58.5, 52.5) * mm});
            skLineSegment(sketch, "E39", {"start": v(38.5, 60) * mm, "end": v(38.5, 45) * mm});
            skSolve(sketch);
        }
        {
            var Q0;
            {var subQ0=sQuery(id+"F29.wireOp",EDGE,"E29");var subQ1=makeQuery(id+"F30.opExtrude","CAP_EDGE",EDGE,{"disambiguationData":[OSD([subQ0])],"isStart":false});Q0=makeQuery(id+"F41.imprint","IMPRINT",FACE,{"disambiguationData":[TD([[makeQuery(id+"F41.imprint","IMPRINT",EDGE,{"derivedFrom":subQ1}),-1.0]])]});}
            extrude(context, id + "F42", {"entities" : qUnion([Q0]), "operationType" : NewBodyOperationType.REMOVE, "oppositeDirection" : true, "depth" : 25 * mm});
        }
    });
